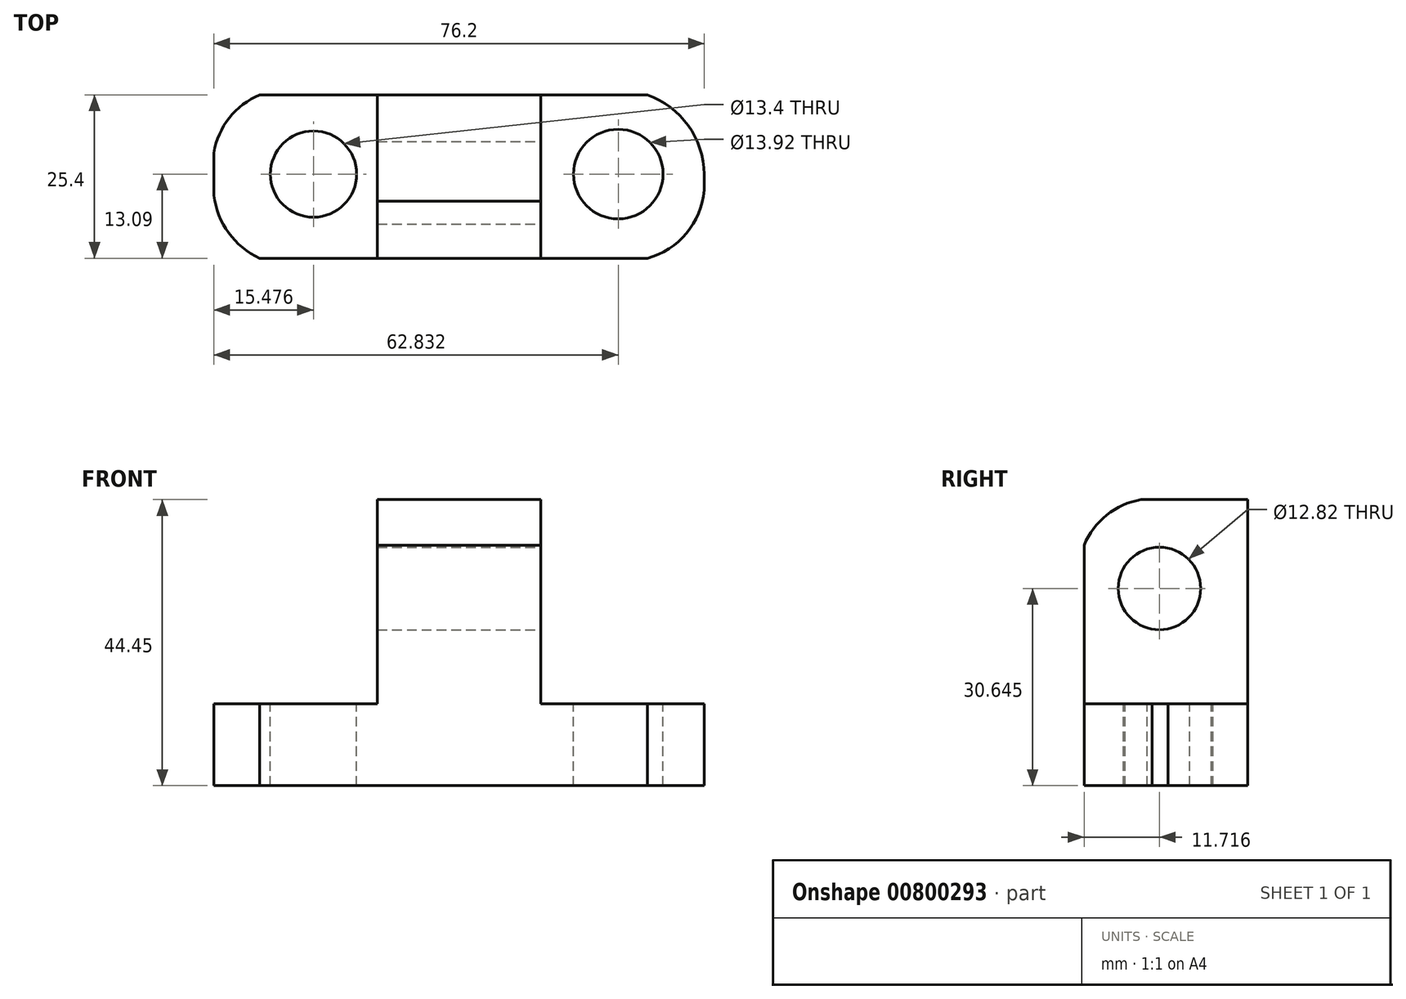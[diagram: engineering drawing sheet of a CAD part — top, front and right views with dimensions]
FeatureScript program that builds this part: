
annotation { "Feature Type Name" : "Feature", "Feature Type Description" : "" }
export const myFeature = defineFeature(function(context is Context, id is Id, definition is map)
    precondition{}
    {
        {
            var Q0;
            Q0=qCreatedBy(makeId("Front.planeOp"),FACE);
            var sketch = newSketch(context, id + "F0", { "sketchPlane" : qUnion([Q0])});
            skLineSegment(sketch, "E0", {"start": v(0, 0) * mm, "end": v(76.2, 0) * mm});
            skLineSegment(sketch, "E1", {"start": v(76.2, 0) * mm, "end": v(76.2, 44.45) * mm});
            skLineSegment(sketch, "E2", {"start": v(76.2, 44.45) * mm, "end": v(0, 44.45) * mm});
            skLineSegment(sketch, "E3", {"start": v(0, 44.45) * mm, "end": v(0, 0) * mm});
            skSolve(sketch);
        }
        {
            var Q0;
            Q0=qSketchRegion(id+"F0",true);
            var Q1;
            Q1=makeQuery(id+"F0.imprint","IMPRINT",FACE,{"disambiguationData":[TD([[makeQuery(id+"F0.imprint","IMPRINT",EDGE,{"derivedFrom":sQuery(id+"F0.wireOp",EDGE,"E0")}),1.0]])]});
            extrude(context, id + "F1", {"entities" : qUnion([Q0, Q1]), "depth" : 25.4 * mm});
        }
        {
            var Q0;
            Q0=makeQuery(id+"F1.opExtrude","CAP_FACE",FACE,{"disambiguationData":[OSD([sQuery(id+"F0.wireOp",EDGE,"E0"),sQuery(id+"F0.wireOp",EDGE,"E1"),sQuery(id+"F0.wireOp",EDGE,"E2"),sQuery(id+"F0.wireOp",EDGE,"E3")])],"isStart":false});
            var sketch = newSketch(context, id + "F2", { "sketchPlane" : qUnion([Q0])});
            skLineSegment(sketch, "E4", {"start": v(0, 12.7) * mm, "end": v(25.4, 12.7) * mm});
            skLineSegment(sketch, "E5", {"start": v(0, 12.7) * mm, "end": v(0, 44.45) * mm});
            skLineSegment(sketch, "E6", {"start": v(0, 44.45) * mm, "end": v(25.4, 44.45) * mm});
            skLineSegment(sketch, "E7", {"start": v(25.4, 44.45) * mm, "end": v(25.4, 12.7) * mm});
            skLineSegment(sketch, "E8", {"start": v(76.2, 12.7) * mm, "end": v(50.8, 12.7) * mm});
            skLineSegment(sketch, "E9", {"start": v(50.8, 12.7) * mm, "end": v(50.8, 44.45) * mm});
            skLineSegment(sketch, "E10", {"start": v(50.8, 44.45) * mm, "end": v(76.2, 44.45) * mm});
            skLineSegment(sketch, "E11", {"start": v(76.2, 44.45) * mm, "end": v(76.2, 12.7) * mm});
            skSolve(sketch);
        }
        {
            var Q0;
            Q0=makeQuery(id+"F2.imprint","IMPRINT",FACE,{"disambiguationData":[TD([[makeQuery(id+"F2.imprint","IMPRINT",EDGE,{"derivedFrom":sQuery(id+"F2.wireOp",EDGE,"E4")}),1.0]])]});
            var Q1;
            Q1=makeQuery(id+"F2.imprint","IMPRINT",FACE,{"disambiguationData":[TD([[makeQuery(id+"F2.imprint","IMPRINT",EDGE,{"derivedFrom":sQuery(id+"F2.wireOp",EDGE,"E8")}),-1.0]])]});
            extrude(context, id + "F3", {"entities" : qUnion([Q0, Q1]), "operationType" : NewBodyOperationType.REMOVE, "oppositeDirection" : true, "depth" : 25.4 * mm});
        }
        {
            var Q0;
            Q0=makeQuery(id+"F3.boolean.opBoolean","COPY",FACE,{"derivedFrom":makeQuery(id+"F3.opExtrude","SWEPT_FACE",FACE,{"disambiguationData":[OSD([sQuery(id+"F2.wireOp",EDGE,"E9")])]})});
            var sketch = newSketch(context, id + "F4", { "sketchPlane" : qUnion([Q0])});
            skArc(sketch, "E12", {"start": v(-12.7, 44.45) * mm, "mid": v(-23.7, 40.24) * mm, "end": v(-25.4, 28.58) * mm});
            skArc(sketch, "E13", {"start": v(0, 28.58) * mm, "mid": v(-2.88, 39.3) * mm, "end": v(-12.7, 44.45) * mm});
            skSolve(sketch);
        }
        {
            var Q0;
            Q0=qSketchRegion(id+"F4",true);
            var Q1;
            {var subQ0=sQuery(id+"F4.wireOp",EDGE,"E12");var subQ1=sQuery(id+"F2.wireOp",EDGE,"E9");var subQ4=makeQuery(id+"F3.boolean.opBoolean","COPY",EDGE,{"derivedFrom":makeQuery(id+"F3.opExtrude","CAP_EDGE",EDGE,{"disambiguationData":[OSD([subQ1])],"isStart":true})});var subQ5=makeQuery(id+"F4.imprint","INTERSECT",VERTEX,{"disambiguationData":[OD(1.0)],"derivedFrom":[subQ4,subQ0]});Q1=makeQuery(id+"F4.imprint","IMPRINT",FACE,{"disambiguationData":[TD([[makeQuery(id+"F4.imprint","IMPRINT",EDGE,{"disambiguationData":[TD([[subQ5,1.0]])],"derivedFrom":subQ0}),-1.0]])]});}
            var Q2;
            {var subQ0=sQuery(id+"F4.wireOp",EDGE,"E13");var subQ1=sQuery(id+"F2.wireOp",EDGE,"E9");var subQ4=makeQuery(id+"F3.boolean.opBoolean","COPY",EDGE,{"derivedFrom":makeQuery(id+"F3.opExtrude","CAP_EDGE",EDGE,{"disambiguationData":[OSD([subQ1])],"isStart":false})});var subQ5=makeQuery(id+"F4.imprint","INTERSECT",VERTEX,{"disambiguationData":[OD(1.0)],"derivedFrom":[subQ4,subQ0]});Q2=makeQuery(id+"F4.imprint","IMPRINT",FACE,{"disambiguationData":[TD([[makeQuery(id+"F4.imprint","IMPRINT",EDGE,{"disambiguationData":[TD([[subQ5,-1.0]])],"derivedFrom":subQ4}),1.0]])]});}
            extrude(context, id + "F5", {"entities" : qUnion([Q0, Q1, Q2]), "operationType" : NewBodyOperationType.REMOVE, "oppositeDirection" : true, "depth" : 25.4 * mm});
        }
        {
            var Q0;
            Q0=makeQuery(id+"F3.boolean.opBoolean","COPY",FACE,{"derivedFrom":makeQuery(id+"F3.opExtrude","SWEPT_FACE",FACE,{"disambiguationData":[OSD([sQuery(id+"F2.wireOp",EDGE,"E9")])]})});
            var sketch = newSketch(context, id + "F6", { "sketchPlane" : qUnion([Q0])});
            skCircle(sketch, "E14", {"center": v(-13.68, 30.65) * mm, "radius": 6.4 * mm});
            skSolve(sketch);
        }
        {
            var Q0;
            Q0=makeQuery(id+"F6.imprint","IMPRINT",FACE,{"disambiguationData":[TD([[makeQuery(id+"F6.imprint","IMPRINT",EDGE,{"derivedFrom":sQuery(id+"F6.wireOp",EDGE,"E14")}),1.0]])]});
            extrude(context, id + "F7", {"entities" : qUnion([Q0]), "operationType" : NewBodyOperationType.REMOVE, "oppositeDirection" : true, "depth" : 25.4 * mm});
        }
        {
            var Q0;
            Q0=makeQuery(id+"F3.boolean.opBoolean","COPY",FACE,{"derivedFrom":makeQuery(id+"F3.opExtrude","SWEPT_FACE",FACE,{"disambiguationData":[OSD([sQuery(id+"F2.wireOp",EDGE,"E4")])]})});
            var sketch = newSketch(context, id + "F8", { "sketchPlane" : qUnion([Q0])});
            skArc(sketch, "E15", {"start": v(0, -12.7) * mm, "mid": v(1.5, -20.2) * mm, "end": v(7.12, -25.4) * mm});
            skArc(sketch, "E16", {"start": v(7.12, 0) * mm, "mid": v(1.35, -5.11) * mm, "end": v(0, -12.7) * mm});
            skPoint(sketch, "E16.startSnap0", {"position": v(12.7, 0) * mm});
            skSolve(sketch);
        }
        {
            var Q0;
            Q0=qSketchRegion(id+"F8",true);
            var Q1;
            {var subQ0=sQuery(id+"F8.wireOp",EDGE,"E16");var subQ1=sQuery(id+"F2.wireOp",EDGE,"E4");var subQ2=makeQuery(id+"F3.boolean.opBoolean","COPY",EDGE,{"derivedFrom":makeQuery(id+"F3.opExtrude","CAP_EDGE",EDGE,{"disambiguationData":[OSD([subQ1])],"isStart":false})});var subQ3=makeQuery(id+"F8.imprint","INTERSECT",VERTEX,{"derivedFrom":[subQ2,subQ0]});Q1=makeQuery(id+"F8.imprint","IMPRINT",FACE,{"disambiguationData":[TD([[makeQuery(id+"F8.imprint","IMPRINT",EDGE,{"disambiguationData":[TD([[subQ3,-1.0]])],"derivedFrom":subQ0}),-1.0]])]});}
            var Q2;
            {var subQ0=sQuery(id+"F8.wireOp",EDGE,"E15");var subQ1=sQuery(id+"F2.wireOp",EDGE,"E4");var subQ2=makeQuery(id+"F3.boolean.opBoolean","COPY",EDGE,{"derivedFrom":makeQuery(id+"F3.opExtrude","CAP_EDGE",EDGE,{"disambiguationData":[OSD([subQ1])],"isStart":true})});var subQ3=makeQuery(id+"F8.imprint","INTERSECT",VERTEX,{"derivedFrom":[subQ2,subQ0]});Q2=makeQuery(id+"F8.imprint","IMPRINT",FACE,{"disambiguationData":[TD([[makeQuery(id+"F8.imprint","IMPRINT",EDGE,{"disambiguationData":[TD([[subQ3,1.0]])],"derivedFrom":subQ0}),-1.0]])]});}
            extrude(context, id + "F9", {"entities" : qUnion([Q0, Q1, Q2]), "operationType" : NewBodyOperationType.REMOVE, "oppositeDirection" : true, "depth" : 25.4 * mm});
        }
        {
            var Q0;
            Q0=makeQuery(id+"F3.boolean.opBoolean","COPY",FACE,{"derivedFrom":makeQuery(id+"F3.opExtrude","SWEPT_FACE",FACE,{"disambiguationData":[OSD([sQuery(id+"F2.wireOp",EDGE,"E8")])]})});
            var sketch = newSketch(context, id + "F10", { "sketchPlane" : qUnion([Q0])});
            skArc(sketch, "E17", {"start": v(67.34, -25.4) * mm, "mid": v(74.08, -20.66) * mm, "end": v(76.2, -12.7) * mm});
            skArc(sketch, "E18", {"start": v(76.2, -12.7) * mm, "mid": v(73.81, -4.92) * mm, "end": v(67.34, 0) * mm});
            skSolve(sketch);
        }
        {
            var Q0;
            {var subQ0=sQuery(id+"F10.wireOp",EDGE,"E18");var subQ1=sQuery(id+"F2.wireOp",EDGE,"E8");var subQ2=makeQuery(id+"F3.boolean.opBoolean","COPY",EDGE,{"derivedFrom":makeQuery(id+"F3.opExtrude","CAP_EDGE",EDGE,{"disambiguationData":[OSD([subQ1])],"isStart":false})});var subQ3=makeQuery(id+"F10.imprint","INTERSECT",VERTEX,{"derivedFrom":[subQ2,subQ0]});Q0=makeQuery(id+"F10.imprint","IMPRINT",FACE,{"disambiguationData":[TD([[makeQuery(id+"F10.imprint","IMPRINT",EDGE,{"disambiguationData":[TD([[subQ3,1.0]])],"derivedFrom":subQ0}),-1.0]])]});}
            var Q1;
            {var subQ0=sQuery(id+"F10.wireOp",EDGE,"E17");var subQ1=sQuery(id+"F2.wireOp",EDGE,"E8");var subQ2=makeQuery(id+"F3.boolean.opBoolean","COPY",EDGE,{"derivedFrom":makeQuery(id+"F3.opExtrude","CAP_EDGE",EDGE,{"disambiguationData":[OSD([subQ1])],"isStart":true})});var subQ3=makeQuery(id+"F10.imprint","INTERSECT",VERTEX,{"derivedFrom":[subQ2,subQ0]});Q1=makeQuery(id+"F10.imprint","IMPRINT",FACE,{"disambiguationData":[TD([[makeQuery(id+"F10.imprint","IMPRINT",EDGE,{"disambiguationData":[TD([[subQ3,-1.0]])],"derivedFrom":subQ0}),-1.0]])]});}
            extrude(context, id + "F11", {"entities" : qUnion([Q0, Q1]), "operationType" : NewBodyOperationType.REMOVE, "oppositeDirection" : true, "depth" : 25.4 * mm});
        }
        {
            var Q0;
            Q0=makeQuery(id+"F3.boolean.opBoolean","COPY",FACE,{"derivedFrom":makeQuery(id+"F3.opExtrude","SWEPT_FACE",FACE,{"disambiguationData":[OSD([sQuery(id+"F2.wireOp",EDGE,"E4")])]})});
            var sketch = newSketch(context, id + "F12", { "sketchPlane" : qUnion([Q0])});
            skCircle(sketch, "E19", {"center": v(15.48, -12.31) * mm, "radius": 6.7 * mm});
            skPoint(sketch, "E19.centerSnap0", {"position": v(0, -12.31) * mm});
            skCircle(sketch, "E20", {"center": v(62.83, -12.31) * mm, "radius": 6.96 * mm});
            skSolve(sketch);
        }
        {
            var Q0;
            Q0=makeQuery(id+"F12.imprint","IMPRINT",FACE,{"disambiguationData":[TD([[makeQuery(id+"F12.imprint","IMPRINT",EDGE,{"derivedFrom":sQuery(id+"F12.wireOp",EDGE,"E20")}),1.0]])]});
            var Q1;
            Q1=makeQuery(id+"F12.imprint","IMPRINT",FACE,{"disambiguationData":[TD([[makeQuery(id+"F12.imprint","IMPRINT",EDGE,{"derivedFrom":sQuery(id+"F12.wireOp",EDGE,"E19")}),1.0]])]});
            extrude(context, id + "F13", {"entities" : qUnion([Q0, Q1]), "operationType" : NewBodyOperationType.REMOVE, "oppositeDirection" : true, "depth" : 25.4 * mm});
        }
    });
